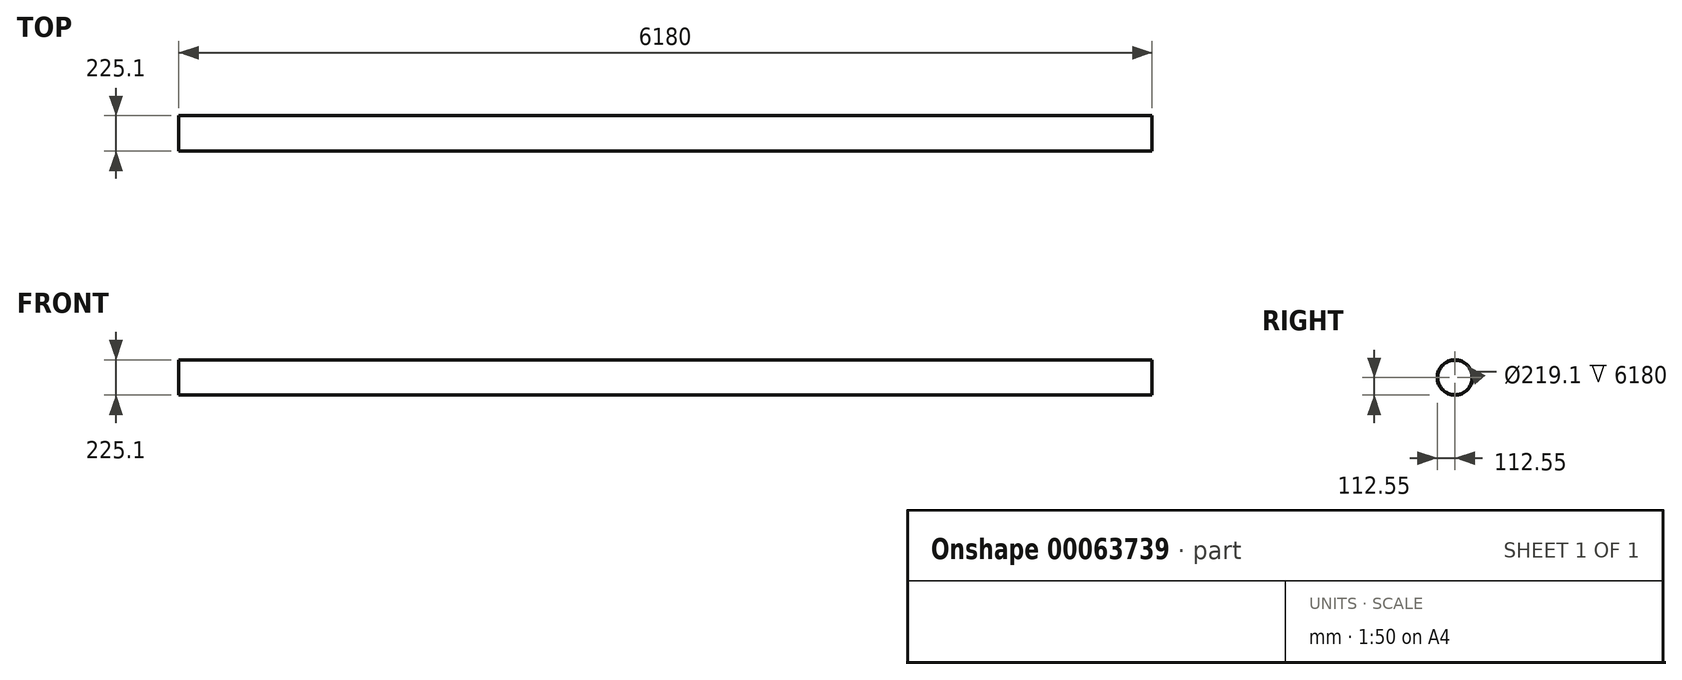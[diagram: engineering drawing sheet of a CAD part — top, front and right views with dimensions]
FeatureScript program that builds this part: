
annotation { "Feature Type Name" : "Feature", "Feature Type Description" : "" }
export const myFeature = defineFeature(function(context is Context, id is Id, definition is map)
    precondition{}
    {
        {
            var Q0;
            Q0=qCreatedBy(makeId("Right.planeOp"),FACE);
            var sketch = newSketch(context, id + "F0", { "sketchPlane" : qUnion([Q0])});
            skCircle(sketch, "E0", {"center": v(0, 0) * mm, "radius": 109.55 * mm});
            skCircle(sketch, "E1", {"center": v(0, 0) * mm, "radius": 112.55 * mm});
            skSolve(sketch);
        }
        {
            var Q0;
            Q0=makeQuery(id+"F0.imprint","IMPRINT",FACE,{"disambiguationData":[TD([[makeQuery(id+"F0.imprint","IMPRINT",EDGE,{"derivedFrom":sQuery(id+"F0.wireOp",EDGE,"E0")}),-1.0]])]});
            extrude(context, id + "F1", {"entities" : qUnion([Q0]), "depth" : 6180 * mm});
        }
    });
